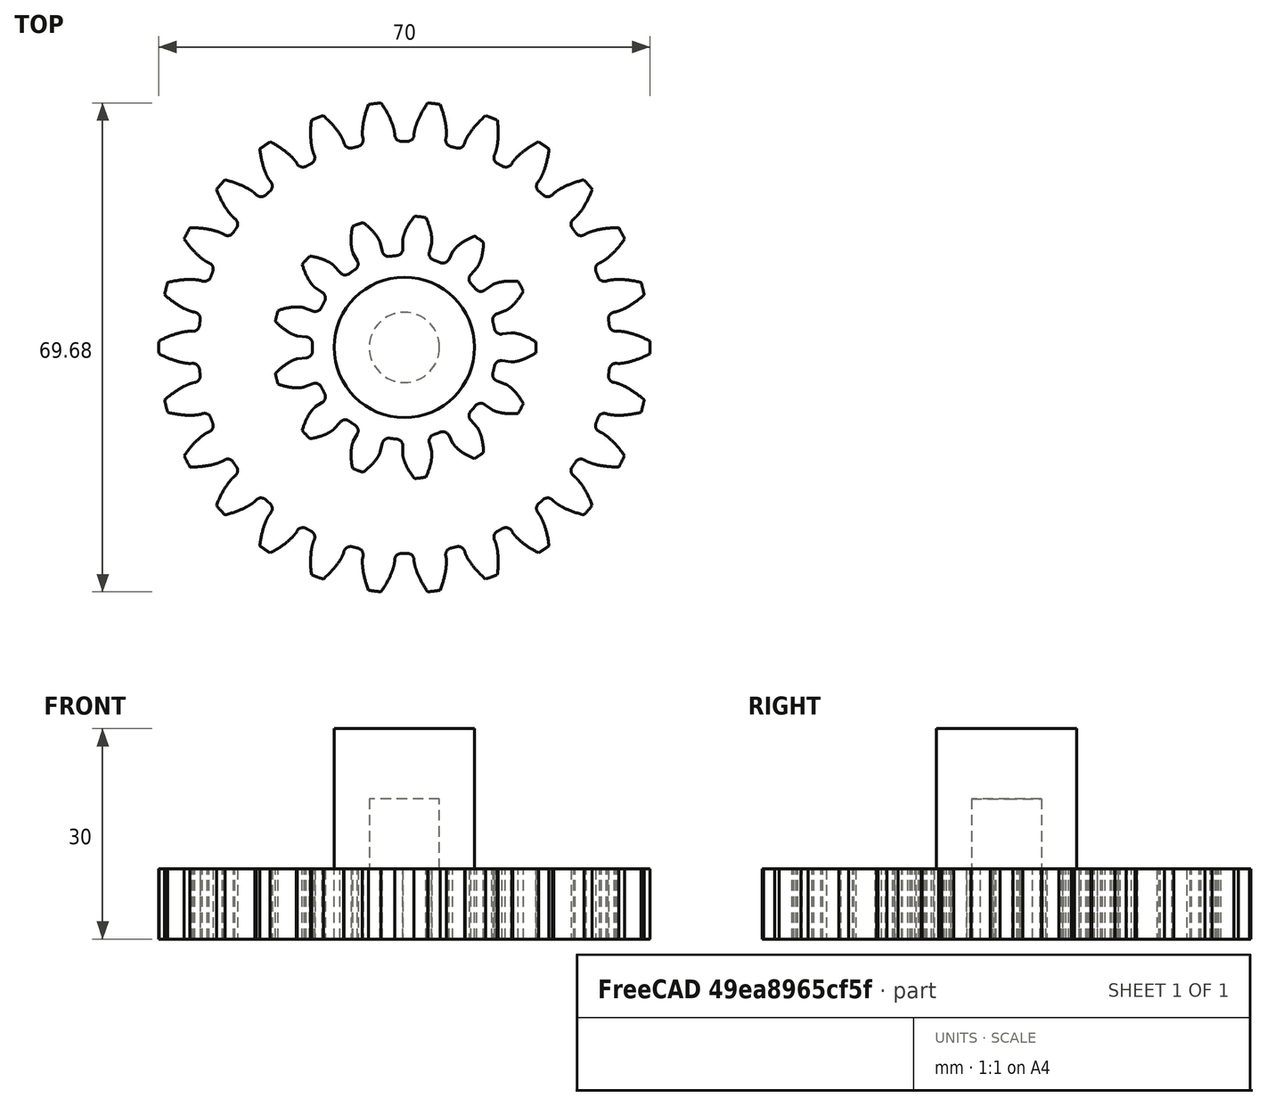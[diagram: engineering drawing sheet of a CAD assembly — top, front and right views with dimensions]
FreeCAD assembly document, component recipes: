
FREECAD ASSEMBLY — COMPONENT RECIPES ("GearAssembly")

This assembly document has 2 components, labeled P0..P1 below (a component is one placed body or linked part). 2 of them carry a construction recipe — the FreeCAD feature program that regenerates the part from scratch, quoted from this document or its linked companion documents; the rest are supplied as boundary geometry only. No exploded tour is included for this assembly.
COMPONENT P0 — recipe-attached ("Gear1", modeled in this document).
Construction recipe (the document's own serialized feature program — sketch geometry with constraints, then the solid features built on it; lengths are millimeters unless a unit is written):

FEATURE [Part::Part2DObjectPython] InvoluteGear  # Draft 2D object (typed FeaturePython)
  AddendumCoefficient = 1
  DedendumCoefficient = 1.25
  ExternalGear = true
  HighPrecision = true
  Modules = 2.5
  NumberOfTeeth = 26
  PressureAngle = 20
  ProfileShiftCoefficient = 0
  RootFilletCoefficient = 0.38
FEATURE [PartDesign::Pad] Pad
  Direction = (0,0,1)
  Length = 10
  Length2 = 10
  Profile = -> InvoluteGear
  ReferenceAxis = -> InvoluteGear [N_Axis]
  Refine = true
  Suppressed = false
  Type = 0
FEATURE [PartDesign::CoordinateSystem] Local_CS
  AttacherType = Attacher::AttachEngine3D
  AttachmentSupport = -> [Pad]
  MapMode = 5
  Placement = pos=(0,0,10) rot=(0,0,1;0rad)
FEATURE [Sketcher::SketchObject] Sketch
  ArcFitTolerance = 0
  AttachmentSupport = -> [XY_Plane]
  FullyConstrained = true
  MakeInternals = false
  MapMode = 5
  sketch-geometry (1):
    g0: Circle CenterX=0 CenterY=0 CenterZ=0 NormalX=0 NormalY=0 NormalZ=1 AngleXU=0 Radius=10
  constraints (2):
    c: Coincident(g0,g-1)
    c: Diameter(g0) = 20
FEATURE [PartDesign::Pad] Pad002
  BaseFeature = -> Pad
  Direction = (0,0,1)
  Length = 30
  Length2 = 10
  Profile = -> Sketch
  ReferenceAxis = -> Sketch [N_Axis]
  Refine = true
  Suppressed = false
  Type = 0
FEATURE [PartDesign::Body] Body  label="Gear1"
  AllowCompound = false
  Group = -> [InvoluteGear,Pad,Local_CS,Sketch,Pad002]
  Origin = -> Origin
  Tip = -> Pad002
COMPONENT P1 — recipe-attached ("Gear2", modeled in this document).
Construction recipe (the document's own serialized feature program — sketch geometry with constraints, then the solid features built on it; lengths are millimeters unless a unit is written):

FEATURE [Part::Part2DObjectPython] InvoluteGear001  label="InvoluteGear2"  # Draft 2D object (typed FeaturePython)
  AddendumCoefficient = 1
  DedendumCoefficient = 1.25
  ExternalGear = true
  HighPrecision = true
  Modules = 2.5
  NumberOfTeeth = 13
  PressureAngle = 20
  ProfileShiftCoefficient = 0
  RootFilletCoefficient = 0.38
FEATURE [PartDesign::Pad] Pad001
  Direction = (0,0,1)
  Length = 10
  Length2 = 10
  Profile = -> InvoluteGear001
  ReferenceAxis = -> InvoluteGear001 [N_Axis]
  Refine = true
  Suppressed = false
  Type = 0
FEATURE [PartDesign::CoordinateSystem] Local_CS001
  AttacherType = Attacher::AttachEngine3D
  AttachmentSupport = -> [Pad001]
  MapMode = 5
  Placement = pos=(0,0,10) rot=(0,0,1;0rad)
FEATURE [Sketcher::SketchObject] Sketch001
  ArcFitTolerance = 0
  AttachmentSupport = -> [XY_Plane001]
  FullyConstrained = true
  MakeInternals = false
  MapMode = 5
  sketch-geometry (1):
    g0: Circle CenterX=0 CenterY=0 CenterZ=0 NormalX=0 NormalY=0 NormalZ=1 AngleXU=0 Radius=5
  constraints (2):
    c: Coincident(g0,g-1)
    c: Diameter(g0) = 10
FEATURE [PartDesign::Pad] Pad003
  BaseFeature = -> Pad001
  Direction = (0,0,1)
  Length = 20
  Length2 = 10
  Profile = -> Sketch001
  ReferenceAxis = -> Sketch001 [N_Axis]
  Refine = true
  Suppressed = false
  Type = 0
FEATURE [PartDesign::Body] Body001  label="Gear2"
  AllowCompound = false
  Group = -> [InvoluteGear001,Pad001,Local_CS001,Sketch001,Pad003]
  Origin = -> Origin001
  Tip = -> Pad003
PROVENANCE & LICENSES
A FreeCAD (.FCStd) document from a public repository crawl; recipes are the document's own serialized feature recipes (and, for linked parts, companion documents' recipes).
License: as declared in the source repository (recorded in the dataset sidecar).
